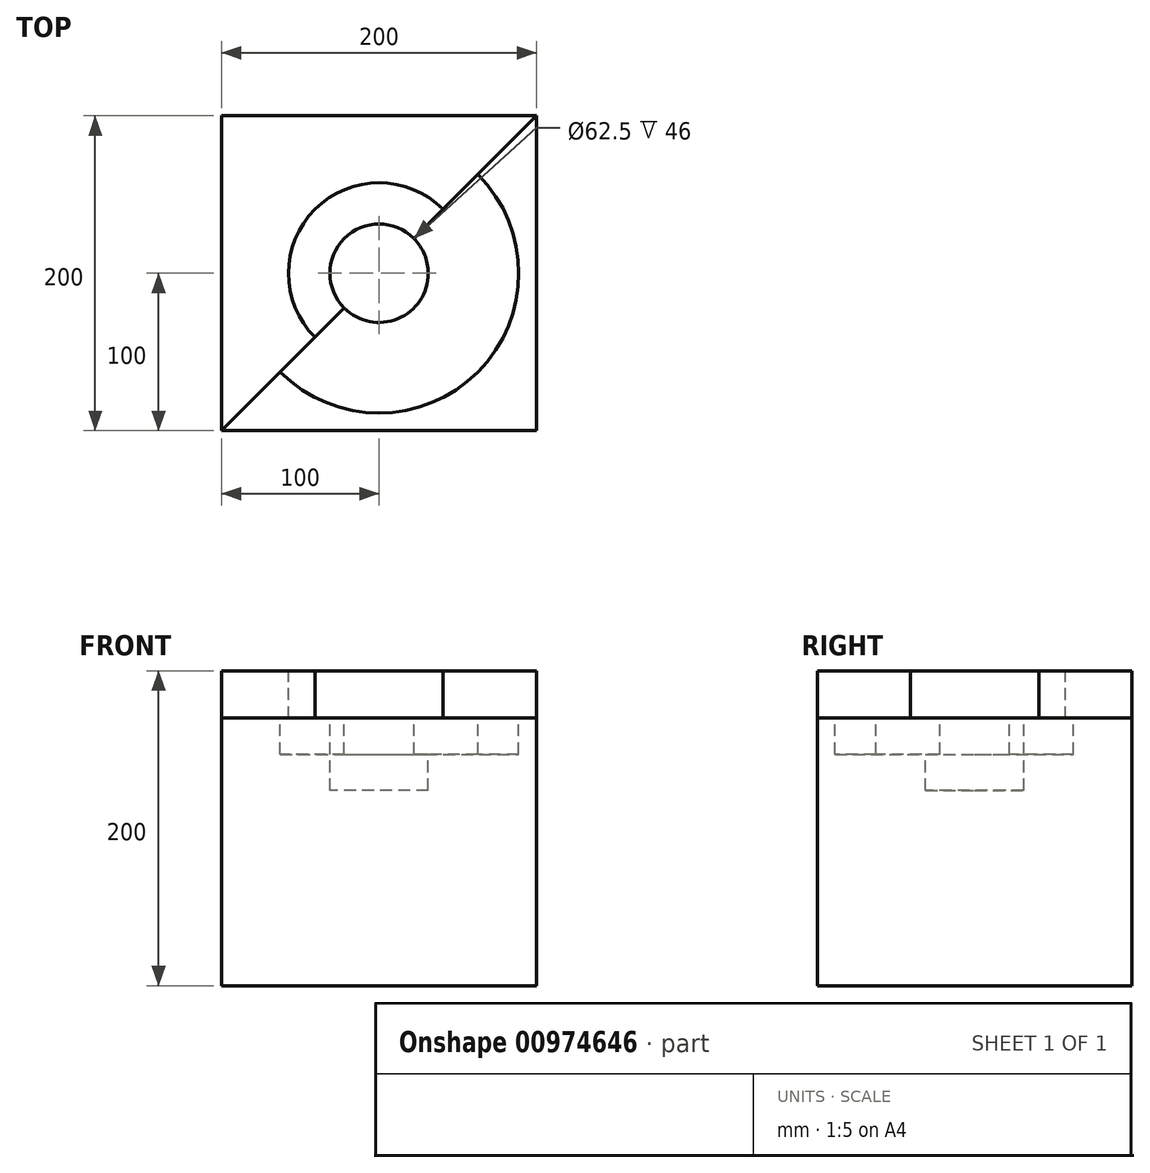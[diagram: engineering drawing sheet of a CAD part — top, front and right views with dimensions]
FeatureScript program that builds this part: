
annotation { "Feature Type Name" : "Feature", "Feature Type Description" : "" }
export const myFeature = defineFeature(function(context is Context, id is Id, definition is map)
    precondition{}
    {
        {
            var Q0;
            Q0=qCreatedBy(makeId("Top.planeOp"),FACE);
            var sketch = newSketch(context, id + "F0", { "sketchPlane" : qUnion([Q0])});
            skLineSegment(sketch, "E0.bottom", {"start": v(100, 100) * mm, "end": v(-100, 100) * mm});
            skLineSegment(sketch, "E0.top", {"start": v(100, -100) * mm, "end": v(-100, -100) * mm});
            skLineSegment(sketch, "E0.left", {"start": v(100, 100) * mm, "end": v(100, -100) * mm});
            skLineSegment(sketch, "E0.right", {"start": v(-100, 100) * mm, "end": v(-100, -100) * mm});
            skPoint(sketch, "E0.middle", {"position": v(0, 0) * mm});
            skSolve(sketch);
        }
        {
            var Q0;
            Q0=makeQuery(id+"F0.imprint","IMPRINT",FACE,{"disambiguationData":[TD([[makeQuery(id+"F0.imprint","IMPRINT",EDGE,{"derivedFrom":sQuery(id+"F0.wireOp",EDGE,"E0.bottom")}),1.0]])]});
            extrude(context, id + "F1", {"entities" : qUnion([Q0]), "depth" : 100 * mm, "offsetDistance" : 25 * mm, "hasSecondDirection" : true, "secondDirectionOppositeDirection" : true, "secondDirectionDepth" : 100 * mm});
        }
        {
            var Q0;
            Q0=makeQuery(id+"F1.opExtrude","CAP_FACE",FACE,{"disambiguationData":[OSD([sQuery(id+"F0.wireOp",EDGE,"E0.bottom"),sQuery(id+"F0.wireOp",EDGE,"E0.top"),sQuery(id+"F0.wireOp",EDGE,"E0.left"),sQuery(id+"F0.wireOp",EDGE,"E0.right")])],"isStart":false});
            var sketch = newSketch(context, id + "F2", { "sketchPlane" : qUnion([Q0])});
            skLineSegment(sketch, "E1", {"start": v(-100, 100) * mm, "end": v(100, -100) * mm});
            skLineSegment(sketch, "E2", {"start": v(100, -100) * mm, "end": v(100, 100) * mm});
            skLineSegment(sketch, "E3", {"start": v(100, 100) * mm, "end": v(-100, -100) * mm});
            skCircle(sketch, "E4", {"center": v(0, 0) * mm, "radius": 88.75 * mm});
            skCircle(sketch, "E5", {"center": v(0, 0) * mm, "radius": 57.5 * mm});
            skCircle(sketch, "E6", {"center": v(0, 0) * mm, "radius": 31.25 * mm});
            skSolve(sketch);
        }
        {
            var Q0;
            {var subQ0=sQuery(id+"F2.wireOp",EDGE,"E3");var subQ1=sQuery(id+"F2.wireOp",EDGE,"E1");var subQ2=makeQuery(id+"F2.imprint","INTERSECT",VERTEX,{"derivedFrom":[subQ1,subQ0]});Q0=makeQuery(id+"F2.imprint","IMPRINT",FACE,{"disambiguationData":[TD([[makeQuery(id+"F2.imprint","IMPRINT",EDGE,{"disambiguationData":[TD([[subQ2,-1.0]])],"derivedFrom":subQ1}),1.0]])]});}
            var Q1;
            {var subQ0=sQuery(id+"F2.wireOp",EDGE,"E3");var subQ1=sQuery(id+"F2.wireOp",EDGE,"E1");var subQ2=makeQuery(id+"F2.imprint","INTERSECT",VERTEX,{"derivedFrom":[subQ1,subQ0]});Q1=makeQuery(id+"F2.imprint","IMPRINT",FACE,{"disambiguationData":[TD([[makeQuery(id+"F2.imprint","IMPRINT",EDGE,{"disambiguationData":[TD([[subQ2,-1.0]])],"derivedFrom":subQ1}),-1.0]])]});}
            var Q2;
            {var subQ0=sQuery(id+"F2.wireOp",EDGE,"E6");var subQ1=sQuery(id+"F2.wireOp",EDGE,"E1");var subQ2=makeQuery(id+"F2.imprint","INTERSECT",VERTEX,{"disambiguationData":[OD(0.0)],"derivedFrom":[subQ1,subQ0]});Q2=makeQuery(id+"F2.imprint","IMPRINT",FACE,{"disambiguationData":[TD([[makeQuery(id+"F2.imprint","IMPRINT",EDGE,{"disambiguationData":[TD([[subQ2,-1.0]])],"derivedFrom":subQ1}),-1.0]])]});}
            var Q3;
            {var subQ0=sQuery(id+"F2.wireOp",EDGE,"E6");var subQ1=sQuery(id+"F2.wireOp",EDGE,"E1");var subQ2=makeQuery(id+"F2.imprint","INTERSECT",VERTEX,{"disambiguationData":[OD(0.0)],"derivedFrom":[subQ1,subQ0]});Q3=makeQuery(id+"F2.imprint","IMPRINT",FACE,{"disambiguationData":[TD([[makeQuery(id+"F2.imprint","IMPRINT",EDGE,{"disambiguationData":[TD([[subQ2,-1.0]])],"derivedFrom":subQ1}),1.0]])]});}
            extrude(context, id + "F3", {"entities" : qUnion([Q0, Q1, Q2, Q3]), "operationType" : NewBodyOperationType.REMOVE, "oppositeDirection" : true, "depth" : 76 * mm, "offsetDistance" : 25 * mm});
        }
        {
            var Q0;
            {var subQ0=sQuery(id+"F2.wireOp",EDGE,"E6");var subQ1=sQuery(id+"F2.wireOp",EDGE,"E1");var subQ2=makeQuery(id+"F2.imprint","INTERSECT",VERTEX,{"disambiguationData":[OD(1.0)],"derivedFrom":[subQ1,subQ0]});Q0=makeQuery(id+"F2.imprint","IMPRINT",FACE,{"disambiguationData":[TD([[makeQuery(id+"F2.imprint","IMPRINT",EDGE,{"disambiguationData":[TD([[subQ2,-1.0]])],"derivedFrom":subQ1}),-1.0]])]});}
            var Q1;
            {var subQ0=sQuery(id+"F2.wireOp",EDGE,"E6");var subQ1=sQuery(id+"F2.wireOp",EDGE,"E1");var subQ2=makeQuery(id+"F2.imprint","INTERSECT",VERTEX,{"disambiguationData":[OD(1.0)],"derivedFrom":[subQ1,subQ0]});Q1=makeQuery(id+"F2.imprint","IMPRINT",FACE,{"disambiguationData":[TD([[makeQuery(id+"F2.imprint","IMPRINT",EDGE,{"disambiguationData":[TD([[subQ2,-1.0]])],"derivedFrom":subQ1}),1.0]])]});}
            var Q2;
            {var subQ0=sQuery(id+"F2.wireOp",EDGE,"E5");var subQ1=sQuery(id+"F2.wireOp",EDGE,"E1");var subQ2=makeQuery(id+"F2.imprint","INTERSECT",VERTEX,{"disambiguationData":[OD(0.0)],"derivedFrom":[subQ1,subQ0]});Q2=makeQuery(id+"F2.imprint","IMPRINT",FACE,{"disambiguationData":[TD([[makeQuery(id+"F2.imprint","IMPRINT",EDGE,{"disambiguationData":[TD([[subQ2,-1.0]])],"derivedFrom":subQ1}),1.0]])]});}
            var Q3;
            {var subQ0=sQuery(id+"F2.wireOp",EDGE,"E5");var subQ1=sQuery(id+"F2.wireOp",EDGE,"E1");var subQ2=makeQuery(id+"F2.imprint","INTERSECT",VERTEX,{"disambiguationData":[OD(0.0)],"derivedFrom":[subQ1,subQ0]});Q3=makeQuery(id+"F2.imprint","IMPRINT",FACE,{"disambiguationData":[TD([[makeQuery(id+"F2.imprint","IMPRINT",EDGE,{"disambiguationData":[TD([[subQ2,-1.0]])],"derivedFrom":subQ1}),-1.0]])]});}
            extrude(context, id + "F4", {"entities" : qUnion([Q0, Q1, Q2, Q3]), "operationType" : NewBodyOperationType.REMOVE, "oppositeDirection" : true, "depth" : 53 * mm, "offsetDistance" : 25 * mm});
        }
        {
            var Q0;
            {var subQ0=sQuery(id+"F2.wireOp",EDGE,"E4");var subQ1=sQuery(id+"F2.wireOp",EDGE,"E1");var subQ2=makeQuery(id+"F2.imprint","INTERSECT",VERTEX,{"disambiguationData":[OD(0.0)],"derivedFrom":[subQ1,subQ0]});Q0=makeQuery(id+"F2.imprint","IMPRINT",FACE,{"disambiguationData":[TD([[makeQuery(id+"F2.imprint","IMPRINT",EDGE,{"disambiguationData":[TD([[subQ2,-1.0]])],"derivedFrom":subQ1}),1.0]])]});}
            var Q1;
            {var subQ0=sQuery(id+"F2.wireOp",EDGE,"E5");var subQ1=sQuery(id+"F2.wireOp",EDGE,"E1");var subQ2=makeQuery(id+"F2.imprint","INTERSECT",VERTEX,{"disambiguationData":[OD(1.0)],"derivedFrom":[subQ1,subQ0]});Q1=makeQuery(id+"F2.imprint","IMPRINT",FACE,{"disambiguationData":[TD([[makeQuery(id+"F2.imprint","IMPRINT",EDGE,{"disambiguationData":[TD([[subQ2,-1.0]])],"derivedFrom":subQ1}),1.0]])]});}
            var Q2;
            {var subQ0=sQuery(id+"F2.wireOp",EDGE,"E4");var subQ1=sQuery(id+"F2.wireOp",EDGE,"E1");var subQ2=makeQuery(id+"F2.imprint","INTERSECT",VERTEX,{"disambiguationData":[OD(0.0)],"derivedFrom":[subQ1,subQ0]});Q2=makeQuery(id+"F2.imprint","IMPRINT",FACE,{"disambiguationData":[TD([[makeQuery(id+"F2.imprint","IMPRINT",EDGE,{"disambiguationData":[TD([[subQ2,-1.0]])],"derivedFrom":subQ1}),-1.0]])]});}
            var Q3;
            {var subQ0=sQuery(id+"F2.wireOp",EDGE,"E5");var subQ1=sQuery(id+"F2.wireOp",EDGE,"E1");var subQ2=makeQuery(id+"F2.imprint","INTERSECT",VERTEX,{"disambiguationData":[OD(1.0)],"derivedFrom":[subQ1,subQ0]});Q3=makeQuery(id+"F2.imprint","IMPRINT",FACE,{"disambiguationData":[TD([[makeQuery(id+"F2.imprint","IMPRINT",EDGE,{"disambiguationData":[TD([[subQ2,-1.0]])],"derivedFrom":subQ1}),-1.0]])]});}
            extrude(context, id + "F5", {"entities" : qUnion([Q0, Q1, Q2, Q3]), "operationType" : NewBodyOperationType.REMOVE, "oppositeDirection" : true, "depth" : 30 * mm, "offsetDistance" : 25 * mm});
        }
        {
            var Q0;
            Q0=qCreatedBy(makeId("Top.planeOp"),FACE);
            var sketch = newSketch(context, id + "F6", { "sketchPlane" : qUnion([Q0])});
            skLineSegment(sketch, "E7", {"start": v(0, 0) * mm, "end": v(179.56, 0) * mm});
            skLineSegment(sketch, "E8", {"start": v(0, 0) * mm, "end": v(0, -207.58) * mm});
            skSolve(sketch);
        }
    });
